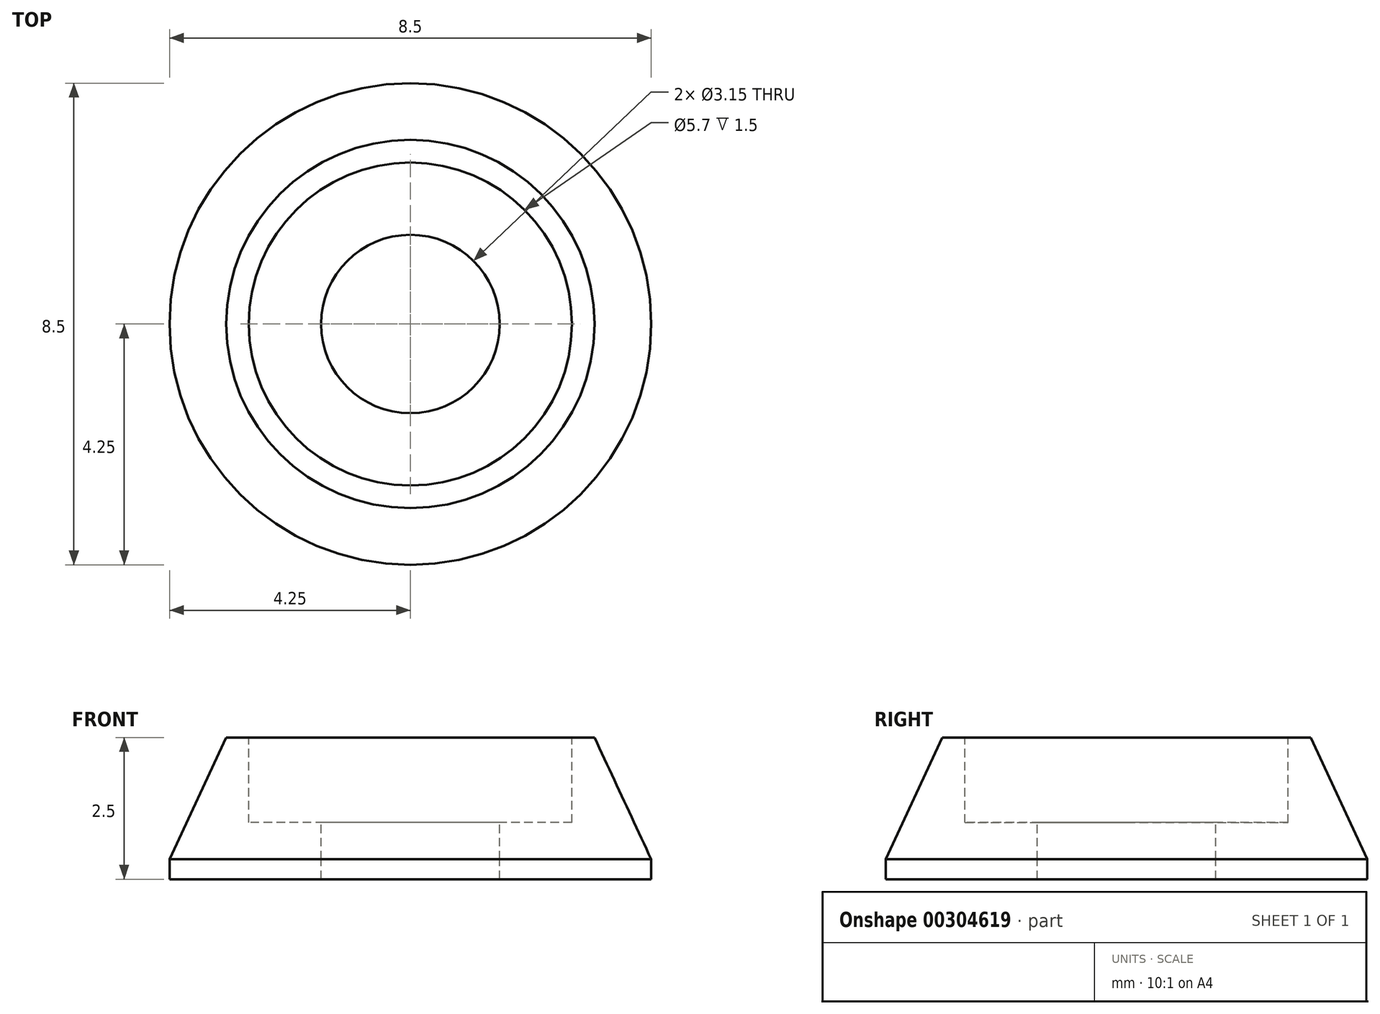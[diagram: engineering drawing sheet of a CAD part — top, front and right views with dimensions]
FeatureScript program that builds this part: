
annotation { "Feature Type Name" : "Feature", "Feature Type Description" : "" }
export const myFeature = defineFeature(function(context is Context, id is Id, definition is map)
    precondition{}
    {
        {
            assignVariable(context, id + "F0", {"name" : "LipHeight", "anyValue" : 0.35 * mm});
        }
        {
            assignVariable(context, id + "F1", {"name" : "WasherHeight", "anyValue" : 1});
        }
        {
            assignVariable(context, id + "F2", {"name" : "PlateauHeight", "anyValue" : 1.5 * mm});
        }
        {
            var Q0;
            Q0=qCreatedBy(makeId("Top.planeOp"),FACE);
            cPlane(context, id + "F3", {"entities" : qUnion([Q0]), "cplaneType" : CPlaneType.OFFSET, "offset" : 0 * mm, "width" : 150 * mm, "height" : 150 * mm});
        }
        {
            var Q0;
            Q0=qCreatedBy(id+"F3.planeOp",FACE);
            cPlane(context, id + "F4", {"entities" : qUnion([Q0]), "cplaneType" : CPlaneType.OFFSET, "offset" : getVariable(context, 'LipHeight'), "width" : 150 * mm, "height" : 150 * mm});
        }
        {
            var Q0;
            Q0=qCreatedBy(id+"F3.planeOp",FACE);
            cPlane(context, id + "F5", {"entities" : qUnion([Q0]), "cplaneType" : CPlaneType.OFFSET, "offset" : (getVariable(context, 'WasherHeight')) * mm, "width" : 150 * mm, "height" : 150 * mm});
        }
        {
            var Q0;
            Q0=qCreatedBy(id+"F5.planeOp",FACE);
            cPlane(context, id + "F6", {"entities" : qUnion([Q0]), "cplaneType" : CPlaneType.OFFSET, "offset" : getVariable(context, 'PlateauHeight'), "width" : 150 * mm, "height" : 150 * mm});
        }
        {
            var Q0;
            Q0=qCreatedBy(makeId("Top.planeOp"),FACE);
            var sketch = newSketch(context, id + "F7", { "sketchPlane" : qUnion([Q0])});
            skCircle(sketch, "E0", {"center": v(0, 0) * mm, "radius": 4.25 * mm});
            skSolve(sketch);
        }
        {
            var Q0;
            Q0=qCreatedBy(id+"F4.planeOp",FACE);
            var sketch = newSketch(context, id + "F8", { "sketchPlane" : qUnion([Q0])});
            skCircle(sketch, "E1.0", {"center": v(0, 0) * mm, "radius": 4.25 * mm});
            skSolve(sketch);
        }
        {
            var Q0;
            Q0=qCreatedBy(id+"F6.planeOp",FACE);
            var sketch = newSketch(context, id + "F9", { "sketchPlane" : qUnion([Q0])});
            skCircle(sketch, "E2", {"center": v(0, 0) * mm, "radius": 2.85 * mm});
            skSolve(sketch);
        }
        {
            var Q0;
            Q0=qCreatedBy(id+"F6.planeOp",FACE);
            var sketch = newSketch(context, id + "F10", { "sketchPlane" : qUnion([Q0])});
            skCircle(sketch, "E3", {"center": v(0, 0) * mm, "radius": 3.25 * mm});
            skSolve(sketch);
        }
        {
            var Q0;
            Q0=qCreatedBy(id+"F5.planeOp",FACE);
            var sketch = newSketch(context, id + "F11", { "sketchPlane" : qUnion([Q0])});
            skCircle(sketch, "E4.0", {"center": v(0, 0) * mm, "radius": 2.85 * mm});
            skSolve(sketch);
        }
        {
            var Q0;
            Q0=qCreatedBy(makeId("Top.planeOp"),FACE);
            var sketch = newSketch(context, id + "F12", { "sketchPlane" : qUnion([Q0])});
            skCircle(sketch, "E5", {"center": v(0, 0) * mm, "radius": 1.57 * mm});
            skSolve(sketch);
        }
        {
            var Q0;
            Q0=qCreatedBy(id+"F5.planeOp",FACE);
            var sketch = newSketch(context, id + "F13", { "sketchPlane" : qUnion([Q0])});
            skCircle(sketch, "E6.0.0", {"center": v(0, 0) * mm, "radius": 1.57 * mm});
            skSolve(sketch);
        }
        {
            var Q0;
            Q0=makeQuery(id+"F7.imprint","IMPRINT",FACE,{"disambiguationData":[TD([[makeQuery(id+"F7.imprint","IMPRINT",EDGE,{"derivedFrom":sQuery(id+"F7.wireOp",EDGE,"E0")}),1.0]])]});
            var Q1;
            Q1=makeQuery(id+"F8.imprint","IMPRINT",FACE,{"disambiguationData":[TD([[makeQuery(id+"F8.imprint","IMPRINT",EDGE,{"derivedFrom":sQuery(id+"F8.wireOp",EDGE,"E1.0")}),1.0]])]});
            loft(context, id + "F14", {"sheetProfilesArray" : [{ "sheetProfileEntities" : qUnion([Q0]) }, { "sheetProfileEntities" : qUnion([Q1]) }]});
        }
        {
            var Q0;
            Q0=qSketchRegion(id+"F10",true);
            var Q1;
            Q1=qSketchRegion(id+"F8",true);
            loft(context, id + "F15", {"sheetProfilesArray" : [{ "sheetProfileEntities" : qUnion([Q0]) }, { "sheetProfileEntities" : qUnion([Q1]) }]});
        }
        {
            var Q1;
            Q1=qSketchRegion(id+"F9",true);
            var Q2;
            Q2=qSketchRegion(id+"F11",true);
            loft(context, id + "F16", {"operationType" : NewBodyOperationType.REMOVE, "sheetProfilesArray" : [{ "sheetProfileEntities" : qUnion([Q1]) }, { "sheetProfileEntities" : qUnion([Q2]) }]});
        }
        {
            var Q1;
            Q1=makeQuery(id+"F13.imprint","IMPRINT",FACE,{"disambiguationData":[TD([[makeQuery(id+"F13.imprint","IMPRINT",EDGE,{"derivedFrom":sQuery(id+"F13.wireOp",EDGE,"E6.0.0")}),1.0]])]});
            var Q2;
            Q2=makeQuery(id+"F12.imprint","IMPRINT",FACE,{"disambiguationData":[TD([[makeQuery(id+"F12.imprint","IMPRINT",EDGE,{"derivedFrom":sQuery(id+"F12.wireOp",EDGE,"E5")}),1.0]])]});
            loft(context, id + "F17", {"operationType" : NewBodyOperationType.REMOVE, "sheetProfilesArray" : [{ "sheetProfileEntities" : qUnion([Q1]) }, { "sheetProfileEntities" : qUnion([Q2]) }]});
        }
    });
